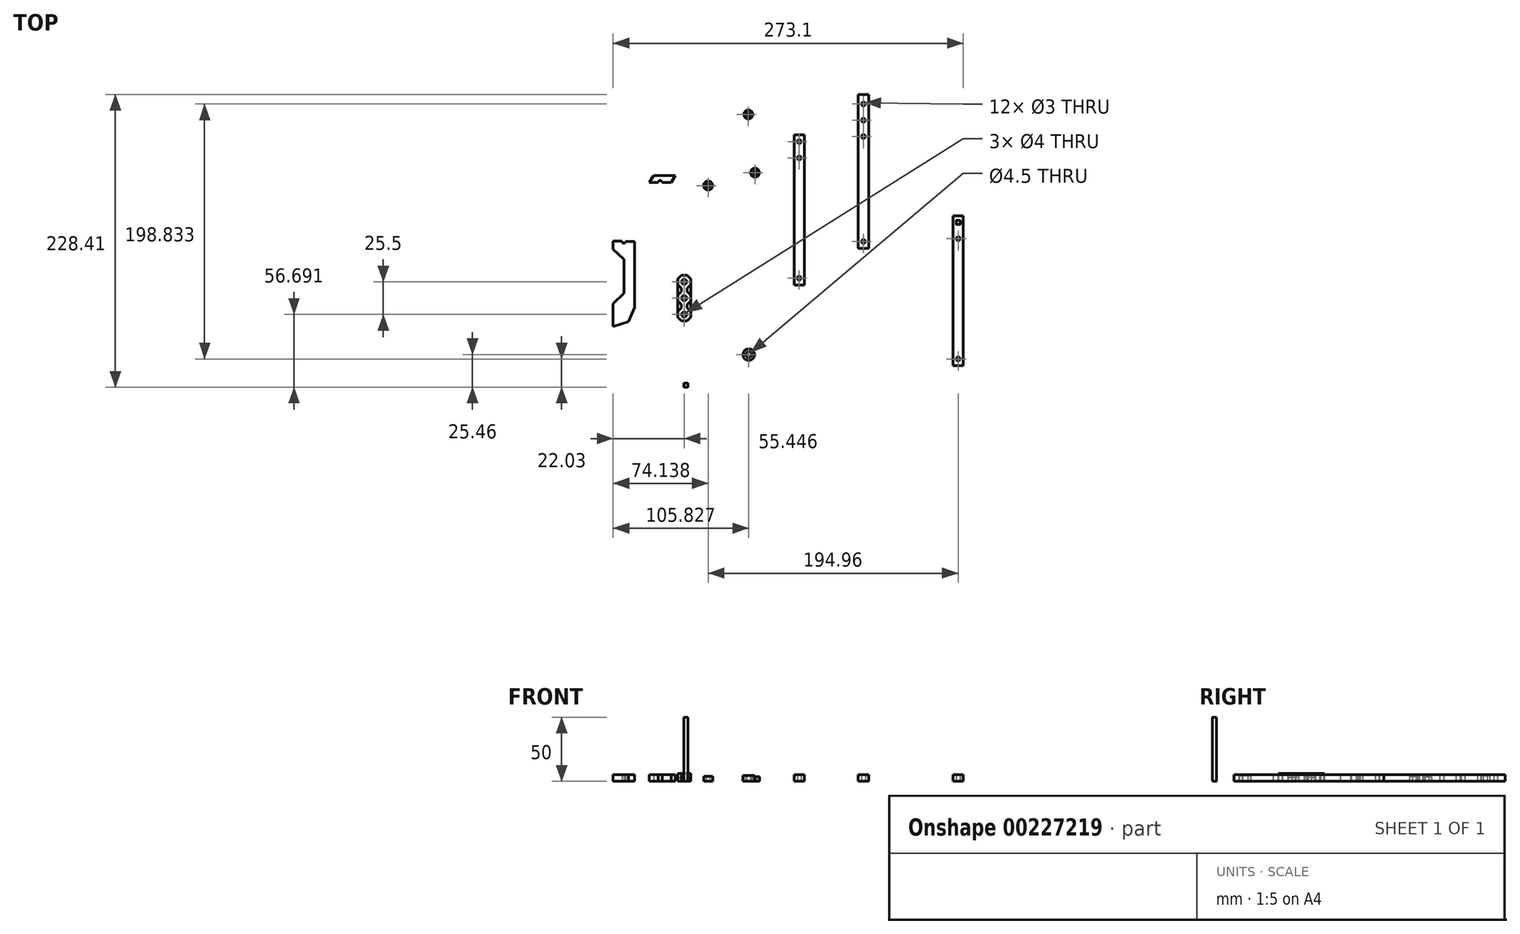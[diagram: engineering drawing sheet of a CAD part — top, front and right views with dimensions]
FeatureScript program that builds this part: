
annotation { "Feature Type Name" : "Feature", "Feature Type Description" : "" }
export const myFeature = defineFeature(function(context is Context, id is Id, definition is map)
    precondition{}
    {
        {
            var Q0;
            Q0=qCreatedBy(makeId("Top.planeOp"),FACE);
            var sketch = newSketch(context, id + "F0", { "sketchPlane" : qUnion([Q0])});
            skLineSegment(sketch, "E0", {"start": v(-67.95, 43.9) * mm, "end": v(-50.95, 43.9) * mm});
            skLineSegment(sketch, "E1", {"start": v(-67.95, 43.9) * mm, "end": v(-99.55, -7.1) * mm});
            skLineSegment(sketch, "E2", {"start": v(-50.95, 43.9) * mm, "end": v(-82.81, -7.53) * mm});
            skLineSegment(sketch, "E3", {"start": v(-99.55, -7.1) * mm, "end": v(-99.55, -13.4) * mm});
            skLineSegment(sketch, "E4", {"start": v(-82.81, -7.53) * mm, "end": v(-82.81, -59.03) * mm});
            skLineSegment(sketch, "E5", {"start": v(-82.81, -59.03) * mm, "end": v(-87.58, -70.04) * mm});
            skLineSegment(sketch, "E6", {"start": v(-87.58, -70.04) * mm, "end": v(-99.57, -73.9) * mm});
            skLineSegment(sketch, "E7", {"start": v(-99.57, -73.9) * mm, "end": v(-99.57, -55.9) * mm});
            skLineSegment(sketch, "E8", {"start": v(-99.55, -13.4) * mm, "end": v(-90.95, -13.4) * mm});
            skLineSegment(sketch, "E9", {"start": v(-90.95, -13.4) * mm, "end": v(-90.95, -55.9) * mm});
            skLineSegment(sketch, "E10", {"start": v(-90.95, -55.9) * mm, "end": v(-99.57, -55.9) * mm});
            skLineSegment(sketch, "E11", {"start": v(-99.55, -13.4) * mm, "end": v(-90.95, -21.4) * mm});
            skLineSegment(sketch, "E12", {"start": v(-99.57, -55.9) * mm, "end": v(-90.95, -47.88) * mm});
            skLineSegment(sketch, "E13", {"start": v(-99.55, -7.1) * mm, "end": v(-82.81, -7.53) * mm});
            skCircle(sketch, "E14", {"center": v(-91.18, -7.32) * mm, "radius": 1.5 * mm});
            skLineSegment(sketch, "E15", {"start": v(-71.24, 38.6) * mm, "end": v(-54.24, 38.6) * mm});
            skCircle(sketch, "E16", {"center": v(-62.74, 38.6) * mm, "radius": 1.5 * mm});
            skLineSegment(sketch, "E17", {"start": v(45.58, 70.38) * mm, "end": v(45.58, -36.08) * mm});
            skCircle(sketch, "E18", {"center": v(45.58, 70.38) * mm, "radius": 1.5 * mm});
            skCircle(sketch, "E19", {"center": v(45.58, -36.08) * mm, "radius": 1.5 * mm});
            skLineSegment(sketch, "E20.bottom", {"start": v(49.58, 75.65) * mm, "end": v(41.58, 75.65) * mm});
            skLineSegment(sketch, "E20.top", {"start": v(49.58, -41.35) * mm, "end": v(41.58, -41.35) * mm});
            skLineSegment(sketch, "E20.left", {"start": v(49.58, 75.65) * mm, "end": v(49.58, -41.35) * mm});
            skLineSegment(sketch, "E20.right", {"start": v(41.58, 75.65) * mm, "end": v(41.58, -41.35) * mm});
            skPoint(sketch, "E20.middle", {"position": v(45.58, 17.15) * mm});
            skLineSegment(sketch, "E21", {"start": v(95.66, 87.02) * mm, "end": v(95.66, -7.48) * mm});
            skCircle(sketch, "E22", {"center": v(95.66, 87.02) * mm, "radius": 1.5 * mm});
            skCircle(sketch, "E23", {"center": v(95.66, -7.48) * mm, "radius": 1.5 * mm});
            skLineSegment(sketch, "E24.bottom", {"start": v(99.66, 92.27) * mm, "end": v(91.66, 92.27) * mm});
            skLineSegment(sketch, "E24.top", {"start": v(99.66, -12.73) * mm, "end": v(91.66, -12.73) * mm});
            skLineSegment(sketch, "E24.left", {"start": v(99.66, 92.27) * mm, "end": v(99.66, -12.73) * mm});
            skLineSegment(sketch, "E24.right", {"start": v(91.66, 92.27) * mm, "end": v(91.66, -12.73) * mm});
            skPoint(sketch, "E24.middle", {"position": v(95.66, 39.77) * mm});
            skCircle(sketch, "E25", {"center": v(-42.75, -119.57) * mm, "radius": 1.5 * mm});
            skCircle(sketch, "E26", {"center": v(5.9, 91.64) * mm, "radius": 1.5 * mm});
            skCircle(sketch, "E27", {"center": v(5.9, 91.64) * mm, "radius": 3.5 * mm});
            skCircle(sketch, "E28", {"center": v(29.29, -65.49) * mm, "radius": 3.14 * mm});
            skLineSegment(sketch, "E29", {"start": v(169.53, -99.11) * mm, "end": v(169.53, 7.39) * mm});
            skLineSegment(sketch, "E30.bottom", {"start": v(173.53, 12.64) * mm, "end": v(165.53, 12.64) * mm});
            skLineSegment(sketch, "E30.top", {"start": v(173.53, -104.36) * mm, "end": v(165.53, -104.36) * mm});
            skLineSegment(sketch, "E30.left", {"start": v(173.53, 12.64) * mm, "end": v(173.53, -104.36) * mm});
            skLineSegment(sketch, "E30.right", {"start": v(165.53, 12.64) * mm, "end": v(165.53, -104.36) * mm});
            skPoint(sketch, "E30.middle", {"position": v(169.53, -45.86) * mm});
            skLineSegment(sketch, "E31.bottom", {"start": v(171.13, 8.99) * mm, "end": v(167.93, 8.99) * mm});
            skLineSegment(sketch, "E31.top", {"start": v(171.13, 5.79) * mm, "end": v(167.93, 5.79) * mm});
            skLineSegment(sketch, "E31.left", {"start": v(171.13, 8.99) * mm, "end": v(171.13, 5.79) * mm});
            skLineSegment(sketch, "E31.right", {"start": v(167.93, 8.99) * mm, "end": v(167.93, 5.79) * mm});
            skPoint(sketch, "E31.middle", {"position": v(169.53, 7.39) * mm});
            skCircle(sketch, "E32", {"center": v(169.53, -99.11) * mm, "radius": 1.5 * mm});
            skLineSegment(sketch, "E33.bottom", {"start": v(-41.18, -121.14) * mm, "end": v(-44.33, -121.14) * mm});
            skLineSegment(sketch, "E33.top", {"start": v(-41.18, -118) * mm, "end": v(-44.33, -118) * mm});
            skLineSegment(sketch, "E33.left", {"start": v(-41.18, -121.14) * mm, "end": v(-41.18, -118) * mm});
            skLineSegment(sketch, "E33.right", {"start": v(-44.33, -121.14) * mm, "end": v(-44.33, -118) * mm});
            skCircle(sketch, "E34", {"center": v(169.53, 7.39) * mm, "radius": 2.1 * mm});
            skLineSegment(sketch, "E35.bottom", {"start": v(165.53, 12.64) * mm, "end": v(173.53, 12.64) * mm});
            skLineSegment(sketch, "E35.top", {"start": v(165.53, 27.64) * mm, "end": v(173.53, 27.64) * mm});
            skLineSegment(sketch, "E35.left", {"start": v(165.53, 12.64) * mm, "end": v(165.53, 27.64) * mm});
            skLineSegment(sketch, "E35.right", {"start": v(173.53, 12.64) * mm, "end": v(173.53, 27.64) * mm});
            skCircle(sketch, "E36", {"center": v(169.53, 20.09) * mm, "radius": 1.5 * mm});
            skPoint(sketch, "E36.centerSnap0", {"position": v(169.53, 12.64) * mm});
            skCircle(sketch, "E37", {"center": v(169.53, -5.31) * mm, "radius": 1.5 * mm});
            skLineSegment(sketch, "E38.bottom", {"start": v(41.58, 75.65) * mm, "end": v(49.58, 75.65) * mm});
            skLineSegment(sketch, "E38.top", {"start": v(41.58, 90.65) * mm, "end": v(49.58, 90.65) * mm});
            skLineSegment(sketch, "E38.left", {"start": v(41.58, 75.65) * mm, "end": v(41.58, 90.65) * mm});
            skLineSegment(sketch, "E38.right", {"start": v(49.58, 75.65) * mm, "end": v(49.58, 90.65) * mm});
            skCircle(sketch, "E39", {"center": v(45.58, 83.08) * mm, "radius": 1.5 * mm});
            skPoint(sketch, "E39.centerSnap0", {"position": v(45.58, 75.65) * mm});
            skCircle(sketch, "E40", {"center": v(45.58, 57.68) * mm, "radius": 1.5 * mm});
            skLineSegment(sketch, "E41", {"start": v(91.66, 92.27) * mm, "end": v(91.66, 107.27) * mm});
            skLineSegment(sketch, "E42", {"start": v(91.66, 107.27) * mm, "end": v(99.66, 107.27) * mm});
            skLineSegment(sketch, "E43", {"start": v(99.66, 107.27) * mm, "end": v(99.66, 92.27) * mm});
            skCircle(sketch, "E44", {"center": v(95.66, 99.72) * mm, "radius": 1.5 * mm});
            skCircle(sketch, "E45", {"center": v(95.66, 74.32) * mm, "radius": 1.5 * mm});
            skCircle(sketch, "E46", {"center": v(6.26, -95.68) * mm, "radius": 2.25 * mm});
            skCircle(sketch, "E47", {"center": v(6.26, -95.68) * mm, "radius": 4.5 * mm});
            skLineSegment(sketch, "E48", {"start": v(-91.18, -7.32) * mm, "end": v(-62.74, -7.32) * mm, "construction": true});
            skLineSegment(sketch, "E49", {"start": v(-62.74, -7.32) * mm, "end": v(-62.74, 38.6) * mm, "construction": true});
            skLineSegment(sketch, "E50", {"start": v(-91.18, -7.32) * mm, "end": v(-62.74, 38.6) * mm, "construction": true});
            skSolve(sketch);
        }
        {
            var Q0;
            Q0=makeQuery(id+"F0.imprint","IMPRINT",FACE,{"disambiguationData":[TD([[makeQuery(id+"F0.imprint","IMPRINT",EDGE,{"derivedFrom":sQuery(id+"F0.wireOp",EDGE,"E0")}),-1.0]])]});
            var Q1;
            {var subQ0=sQuery(id+"F0.wireOp",EDGE,"E8");Q1=makeQuery(id+"F0.imprint","IMPRINT",FACE,{"disambiguationData":[TD([[makeQuery(id+"F0.imprint","IMPRINT",EDGE,{"derivedFrom":subQ0}),-1.0]])]});}
            var Q2;
            {var subQ0=sQuery(id+"F0.wireOp",EDGE,"E10");Q2=makeQuery(id+"F0.imprint","IMPRINT",FACE,{"disambiguationData":[TD([[makeQuery(id+"F0.imprint","IMPRINT",EDGE,{"derivedFrom":subQ0}),-1.0]])]});}
            var Q3;
            {var subQ0=sQuery(id+"F0.wireOp",EDGE,"E13");var subQ3=sQuery(id+"F0.wireOp",EDGE,"E14");var subQ12=makeQuery(id+"F0.imprint","INTERSECT",VERTEX,{"disambiguationData":[OD(0.0)],"derivedFrom":[subQ0,subQ3]});Q3=makeQuery(id+"F0.imprint","IMPRINT",FACE,{"disambiguationData":[TD([[makeQuery(id+"F0.imprint","IMPRINT",EDGE,{"disambiguationData":[TD([[subQ12,1.0]])],"derivedFrom":subQ3}),-1.0]])]});}
            var Q4;
            {var subQ5=sQuery(id+"F0.wireOp",EDGE,"E3");Q4=makeQuery(id+"F0.imprint","IMPRINT",FACE,{"disambiguationData":[TD([[makeQuery(id+"F0.imprint","IMPRINT",EDGE,{"derivedFrom":subQ5}),1.0]])]});}
            var Q5;
            Q5=makeQuery(id+"F0.imprint","IMPRINT",FACE,{"disambiguationData":[TD([[makeQuery(id+"F0.imprint","IMPRINT",EDGE,{"derivedFrom":sQuery(id+"F0.wireOp",EDGE,"E18")}),-1.0]])]});
            var Q6;
            Q6=makeQuery(id+"F0.imprint","IMPRINT",FACE,{"disambiguationData":[TD([[makeQuery(id+"F0.imprint","IMPRINT",EDGE,{"derivedFrom":sQuery(id+"F0.wireOp",EDGE,"E22")}),-1.0]])]});
            var Q7;
            {var subQ0=sQuery(id+"F0.wireOp",EDGE,"E34");var subQ1=sQuery(id+"F0.wireOp",EDGE,"E31.bottom");var subQ2=makeQuery(id+"F0.imprint","INTERSECT",VERTEX,{"disambiguationData":[OD(0.0)],"derivedFrom":[subQ1,subQ0]});Q7=makeQuery(id+"F0.imprint","IMPRINT",FACE,{"disambiguationData":[TD([[makeQuery(id+"F0.imprint","IMPRINT",EDGE,{"disambiguationData":[TD([[subQ2,-1.0]])],"derivedFrom":subQ1}),-1.0]])]});}
            var Q8;
            {var subQ0=sQuery(id+"F0.wireOp",EDGE,"E34");var subQ1=sQuery(id+"F0.wireOp",EDGE,"E31.right");var subQ2=makeQuery(id+"F0.imprint","INTERSECT",VERTEX,{"disambiguationData":[OD(0.0)],"derivedFrom":[subQ1,subQ0]});Q8=makeQuery(id+"F0.imprint","IMPRINT",FACE,{"disambiguationData":[TD([[makeQuery(id+"F0.imprint","IMPRINT",EDGE,{"disambiguationData":[TD([[subQ2,-1.0]])],"derivedFrom":subQ1}),-1.0]])]});}
            var Q9;
            {var subQ0=sQuery(id+"F0.wireOp",EDGE,"E34");var subQ1=sQuery(id+"F0.wireOp",EDGE,"E31.left");var subQ2=makeQuery(id+"F0.imprint","INTERSECT",VERTEX,{"disambiguationData":[OD(0.0)],"derivedFrom":[subQ1,subQ0]});Q9=makeQuery(id+"F0.imprint","IMPRINT",FACE,{"disambiguationData":[TD([[makeQuery(id+"F0.imprint","IMPRINT",EDGE,{"disambiguationData":[TD([[subQ2,-1.0]])],"derivedFrom":subQ1}),1.0]])]});}
            var Q10;
            {var subQ0=sQuery(id+"F0.wireOp",EDGE,"E31.top");var subQ1=sQuery(id+"F0.wireOp",EDGE,"E29");var subQ2=makeQuery(id+"F0.imprint","INTERSECT",VERTEX,{"derivedFrom":[subQ1,subQ0]});Q10=makeQuery(id+"F0.imprint","IMPRINT",FACE,{"disambiguationData":[TD([[makeQuery(id+"F0.imprint","IMPRINT",EDGE,{"disambiguationData":[TD([[subQ2,1.0]])],"derivedFrom":subQ1}),-1.0]])]});}
            var Q11;
            {var subQ0=sQuery(id+"F0.wireOp",EDGE,"E31.top");var subQ1=sQuery(id+"F0.wireOp",EDGE,"E29");var subQ2=makeQuery(id+"F0.imprint","INTERSECT",VERTEX,{"derivedFrom":[subQ1,subQ0]});Q11=makeQuery(id+"F0.imprint","IMPRINT",FACE,{"disambiguationData":[TD([[makeQuery(id+"F0.imprint","IMPRINT",EDGE,{"disambiguationData":[TD([[subQ2,1.0]])],"derivedFrom":subQ1}),1.0]])]});}
            var Q12;
            Q12=makeQuery(id+"F0.imprint","IMPRINT",FACE,{"disambiguationData":[TD([[makeQuery(id+"F0.imprint","IMPRINT",EDGE,{"derivedFrom":sQuery(id+"F0.wireOp",EDGE,"E30.bottom")}),1.0]])]});
            var Q13;
            {var subQ0=sQuery(id+"F0.wireOp",EDGE,"E31.left");var subQ1=sQuery(id+"F0.wireOp",EDGE,"E31.bottom");var subQ2=makeQuery(id+"F0.imprint","INTERSECT",VERTEX,{"derivedFrom":[subQ1,subQ0]});Q13=makeQuery(id+"F0.imprint","IMPRINT",FACE,{"disambiguationData":[TD([[makeQuery(id+"F0.imprint","IMPRINT",EDGE,{"disambiguationData":[TD([[subQ2,-1.0]])],"derivedFrom":subQ1}),1.0]])]});}
            var Q14;
            {var subQ0=sQuery(id+"F0.wireOp",EDGE,"E31.right");var subQ1=sQuery(id+"F0.wireOp",EDGE,"E31.bottom");var subQ2=makeQuery(id+"F0.imprint","INTERSECT",VERTEX,{"derivedFrom":[subQ1,subQ0]});Q14=makeQuery(id+"F0.imprint","IMPRINT",FACE,{"disambiguationData":[TD([[makeQuery(id+"F0.imprint","IMPRINT",EDGE,{"disambiguationData":[TD([[subQ2,1.0]])],"derivedFrom":subQ1}),1.0]])]});}
            var Q15;
            {var subQ0=sQuery(id+"F0.wireOp",EDGE,"E31.right");var subQ1=sQuery(id+"F0.wireOp",EDGE,"E31.top");var subQ2=makeQuery(id+"F0.imprint","INTERSECT",VERTEX,{"derivedFrom":[subQ1,subQ0]});Q15=makeQuery(id+"F0.imprint","IMPRINT",FACE,{"disambiguationData":[TD([[makeQuery(id+"F0.imprint","IMPRINT",EDGE,{"disambiguationData":[TD([[subQ2,1.0]])],"derivedFrom":subQ1}),-1.0]])]});}
            var Q16;
            {var subQ0=sQuery(id+"F0.wireOp",EDGE,"E31.left");var subQ1=sQuery(id+"F0.wireOp",EDGE,"E31.top");var subQ2=makeQuery(id+"F0.imprint","INTERSECT",VERTEX,{"derivedFrom":[subQ1,subQ0]});Q16=makeQuery(id+"F0.imprint","IMPRINT",FACE,{"disambiguationData":[TD([[makeQuery(id+"F0.imprint","IMPRINT",EDGE,{"disambiguationData":[TD([[subQ2,-1.0]])],"derivedFrom":subQ1}),-1.0]])]});}
            var Q17;
            Q17=makeQuery(id+"F0.imprint","IMPRINT",FACE,{"disambiguationData":[TD([[makeQuery(id+"F0.imprint","IMPRINT",EDGE,{"derivedFrom":sQuery(id+"F0.wireOp",EDGE,"E35.bottom")}),1.0]])]});
            var Q18;
            Q18=makeQuery(id+"F0.imprint","IMPRINT",FACE,{"disambiguationData":[TD([[makeQuery(id+"F0.imprint","IMPRINT",EDGE,{"derivedFrom":sQuery(id+"F0.wireOp",EDGE,"E30.top")}),-1.0]])]});
            var Q19;
            Q19=makeQuery(id+"F0.imprint","IMPRINT",FACE,{"disambiguationData":[TD([[makeQuery(id+"F0.imprint","IMPRINT",EDGE,{"derivedFrom":sQuery(id+"F0.wireOp",EDGE,"E38.bottom")}),1.0]])]});
            var Q20;
            Q20=makeQuery(id+"F0.imprint","IMPRINT",FACE,{"disambiguationData":[TD([[makeQuery(id+"F0.imprint","IMPRINT",EDGE,{"derivedFrom":sQuery(id+"F0.wireOp",EDGE,"E24.bottom")}),-1.0]])]});
            extrude(context, id + "F1", {"entities" : qUnion([Q0, Q1, Q2, Q3, Q4, Q5, Q6, Q7, Q8, Q9, Q10, Q11, Q12, Q13, Q14, Q15, Q16, Q17, Q18, Q19, Q20]), "depth" : 5.08 * mm});
        }
        {
            var Q0;
            Q0=makeQuery(id+"F0.imprint","IMPRINT",FACE,{"disambiguationData":[TD([[makeQuery(id+"F0.imprint","IMPRINT",EDGE,{"derivedFrom":sQuery(id+"F0.wireOp",EDGE,"E25")}),1.0]])]});
            var Q1;
            Q1=makeQuery(id+"F0.imprint","IMPRINT",FACE,{"disambiguationData":[TD([[makeQuery(id+"F0.imprint","IMPRINT",EDGE,{"derivedFrom":sQuery(id+"F0.wireOp",EDGE,"E25")}),-1.0]])]});
            extrude(context, id + "F2", {"entities" : qUnion([Q0, Q1]), "depth" : 50 * mm});
        }
        {
            var Q0;
            Q0=makeQuery(id+"F0.imprint","IMPRINT",FACE,{"disambiguationData":[TD([[makeQuery(id+"F0.imprint","IMPRINT",EDGE,{"derivedFrom":sQuery(id+"F0.wireOp",EDGE,"E26")}),-1.0]])]});
            var Q1;
            Q1 = qSketchRegion(id + "F5", true);
            var Q2;
            Q2=makeQuery(id+"F0.imprint","IMPRINT",FACE,{"disambiguationData":[TD([[makeQuery(id+"F0.imprint","IMPRINT",EDGE,{"derivedFrom":sQuery(id+"F0.wireOp",EDGE,"E46")}),-1.0]])]});
            extrude(context, id + "F3", {"entities" : qUnion([Q0, Q1, Q2]), "depth" : 4.45 * mm});
        }
        {
            var Q0;
            Q0=makeQuery(id+"F2.opExtrude","SWEPT_EDGE",EDGE,{"disambiguationData":[OSD([sQuery(id+"F0.wireOp",EDGE,"E33.bottom"),sQuery(id+"F0.wireOp",EDGE,"E33.left")])]});
            var Q1;
            Q1=makeQuery(id+"F2.opExtrude","SWEPT_EDGE",EDGE,{"disambiguationData":[OSD([sQuery(id+"F0.wireOp",EDGE,"E33.top"),sQuery(id+"F0.wireOp",EDGE,"E33.right")])]});
            var Q2;
            Q2=makeQuery(id+"F2.opExtrude","SWEPT_EDGE",EDGE,{"disambiguationData":[OSD([sQuery(id+"F0.wireOp",EDGE,"E33.bottom"),sQuery(id+"F0.wireOp",EDGE,"E33.right")])]});
            var Q3;
            Q3=makeQuery(id+"F2.opExtrude","SWEPT_EDGE",EDGE,{"disambiguationData":[OSD([sQuery(id+"F0.wireOp",EDGE,"E33.top"),sQuery(id+"F0.wireOp",EDGE,"E33.left")])]});
            fillet(context, id + "F4", {"entities" : qUnion([Q0, Q1, Q2, Q3]), "radius" : 0.25 * mm, "tangentPropagation" : true, "allowEdgeOverflow" : false});
        }
        {
            var Q0;
            Q0=qCreatedBy(makeId("Top.planeOp"),FACE);
            var sketch = newSketch(context, id + "F5", { "sketchPlane" : qUnion([Q0])});
            skCircle(sketch, "E51", {"center": v(-25.43, 36.16) * mm, "radius": 3.5 * mm});
            skCircle(sketch, "E52", {"center": v(-25.43, 36.16) * mm, "radius": 1.5 * mm});
            skCircle(sketch, "E53", {"center": v(11.1, 46.21) * mm, "radius": 3.5 * mm});
            skCircle(sketch, "E54", {"center": v(11.1, 46.21) * mm, "radius": 1.5 * mm});
            skSolve(sketch);
        }
        {
            var Q0;
            Q0=makeQuery(id+"F5.imprint","IMPRINT",FACE,{"disambiguationData":[TD([[makeQuery(id+"F5.imprint","IMPRINT",EDGE,{"derivedFrom":sQuery(id+"F5.wireOp",EDGE,"E51")}),1.0]])]});
            extrude(context, id + "F6", {"entities" : qUnion([Q0]), "depth" : 3.81 * mm});
        }
        {
            var Q0;
            Q0=qCreatedBy(makeId("Top.planeOp"),FACE);
            var sketch = newSketch(context, id + "F7", { "sketchPlane" : qUnion([Q0])});
            skCircle(sketch, "E55", {"center": v(-44.12, -38.95) * mm, "radius": 2 * mm});
            skCircle(sketch, "E56", {"center": v(-44.12, -51.7) * mm, "radius": 2 * mm});
            skCircle(sketch, "E57", {"center": v(-44.12, -64.45) * mm, "radius": 2 * mm});
            skLineSegment(sketch, "E58", {"start": v(-44.12, -51.7) * mm, "end": v(-44.12, -38.95) * mm});
            skLineSegment(sketch, "E59", {"start": v(-44.12, -51.7) * mm, "end": v(-44.12, -64.45) * mm});
            skLineSegment(sketch, "E60", {"start": v(-46.37, -33.85) * mm, "end": v(-41.87, -33.85) * mm});
            skLineSegment(sketch, "E61", {"start": v(-49.22, -41.2) * mm, "end": v(-49.22, -36.7) * mm});
            skLineSegment(sketch, "E62.MirrorCS", {"start": v(-39.02, -41.2) * mm, "end": v(-39.02, -36.7) * mm});
            skLineSegment(sketch, "E63", {"start": v(-49.22, -36.7) * mm, "end": v(-46.37, -33.85) * mm});
            skLineSegment(sketch, "E64", {"start": v(-41.87, -33.85) * mm, "end": v(-39.02, -36.7) * mm});
            skLineSegment(sketch, "E65", {"start": v(-44.12, -38.95) * mm, "end": v(-39.02, -38.95) * mm});
            skPoint(sketch, "E65.endSnap0", {"position": v(-39.02, -38.94) * mm});
            skLineSegment(sketch, "E66.MirrorCS", {"start": v(-46.37, -44.05) * mm, "end": v(-41.87, -44.05) * mm});
            skLineSegment(sketch, "E67", {"start": v(-49.22, -41.2) * mm, "end": v(-46.37, -44.05) * mm});
            skLineSegment(sketch, "E68", {"start": v(-41.87, -44.05) * mm, "end": v(-39.02, -41.2) * mm});
            skPoint(sketch, "E69.endSnap0", {"position": v(-44.12, -45.32) * mm});
            skLineSegment(sketch, "E70.MirrorCS", {"start": v(-46.37, -46.6) * mm, "end": v(-41.87, -46.6) * mm});
            skLineSegment(sketch, "E71.MirrorCS", {"start": v(-41.87, -46.6) * mm, "end": v(-39.02, -49.46) * mm});
            skLineSegment(sketch, "E72.MirrorCS", {"start": v(-49.22, -49.46) * mm, "end": v(-46.37, -46.6) * mm});
            skLineSegment(sketch, "E73.MirrorCS", {"start": v(-49.22, -49.46) * mm, "end": v(-49.22, -53.96) * mm});
            skLineSegment(sketch, "E74.MirrorCS", {"start": v(-49.22, -53.96) * mm, "end": v(-46.37, -56.8) * mm});
            skLineSegment(sketch, "E75.MirrorCS", {"start": v(-46.37, -56.8) * mm, "end": v(-41.87, -56.8) * mm});
            skLineSegment(sketch, "E76.MirrorCS", {"start": v(-41.87, -56.8) * mm, "end": v(-39.02, -53.96) * mm});
            skLineSegment(sketch, "E77.MirrorCS", {"start": v(-39.02, -49.46) * mm, "end": v(-39.02, -53.96) * mm});
            skLineSegment(sketch, "E78.MirrorCS", {"start": v(-46.37, -59.35) * mm, "end": v(-41.87, -59.35) * mm});
            skLineSegment(sketch, "E79.MirrorCS", {"start": v(-41.87, -59.35) * mm, "end": v(-39.02, -62.2) * mm});
            skLineSegment(sketch, "E80.MirrorCS", {"start": v(-39.02, -66.7) * mm, "end": v(-39.02, -62.2) * mm});
            skLineSegment(sketch, "E81.MirrorCS", {"start": v(-41.87, -69.55) * mm, "end": v(-39.02, -66.7) * mm});
            skLineSegment(sketch, "E82.MirrorCS", {"start": v(-49.22, -62.2) * mm, "end": v(-46.37, -59.35) * mm});
            skLineSegment(sketch, "E83.MirrorCS", {"start": v(-49.22, -66.7) * mm, "end": v(-49.22, -62.2) * mm});
            skLineSegment(sketch, "E84.MirrorCS", {"start": v(-49.22, -66.7) * mm, "end": v(-46.37, -69.55) * mm});
            skLineSegment(sketch, "E85.MirrorCS", {"start": v(-46.37, -69.55) * mm, "end": v(-41.87, -69.55) * mm});
            skLineSegment(sketch, "E86", {"start": v(-46.37, -46.6) * mm, "end": v(-46.37, -44.05) * mm});
            skLineSegment(sketch, "E87", {"start": v(-41.87, -44.05) * mm, "end": v(-41.87, -46.6) * mm});
            skLineSegment(sketch, "E88", {"start": v(-46.37, -56.8) * mm, "end": v(-46.37, -59.35) * mm});
            skLineSegment(sketch, "E89", {"start": v(-41.87, -56.8) * mm, "end": v(-41.87, -59.35) * mm});
            skLineSegment(sketch, "E90", {"start": v(-49.22, -49.46) * mm, "end": v(-49.22, -41.2) * mm});
            skLineSegment(sketch, "E91", {"start": v(-39.02, -41.2) * mm, "end": v(-39.02, -49.46) * mm});
            skLineSegment(sketch, "E92", {"start": v(-39.02, -53.96) * mm, "end": v(-39.02, -62.2) * mm});
            skLineSegment(sketch, "E93", {"start": v(-49.22, -53.96) * mm, "end": v(-49.22, -62.2) * mm});
            skSolve(sketch);
        }
        {
            var Q0;
            Q0=makeQuery(id+"F7.imprint","IMPRINT",FACE,{"disambiguationData":[TD([[makeQuery(id+"F7.imprint","IMPRINT",EDGE,{"derivedFrom":sQuery(id+"F7.wireOp",EDGE,"E68")}),-1.0]])]});
            var Q1;
            Q1=makeQuery(id+"F7.imprint","IMPRINT",FACE,{"disambiguationData":[TD([[makeQuery(id+"F7.imprint","IMPRINT",EDGE,{"derivedFrom":sQuery(id+"F7.wireOp",EDGE,"E67")}),-1.0]])]});
            var Q2;
            Q2=makeQuery(id+"F7.imprint","IMPRINT",FACE,{"disambiguationData":[TD([[makeQuery(id+"F7.imprint","IMPRINT",EDGE,{"derivedFrom":sQuery(id+"F7.wireOp",EDGE,"E74.MirrorCS")}),-1.0]])]});
            var Q3;
            Q3=makeQuery(id+"F7.imprint","IMPRINT",FACE,{"disambiguationData":[TD([[makeQuery(id+"F7.imprint","IMPRINT",EDGE,{"derivedFrom":sQuery(id+"F7.wireOp",EDGE,"E76.MirrorCS")}),-1.0]])]});
            extrude(context, id + "F8", {"entities" : qUnion([Q0, Q1, Q2, Q3]), "depth" : 3.1 * mm});
        }
        {
            var Q0;
            Q0=makeQuery(id+"F7.imprint","IMPRINT",FACE,{"disambiguationData":[TD([[makeQuery(id+"F7.imprint","IMPRINT",EDGE,{"derivedFrom":sQuery(id+"F7.wireOp",EDGE,"E60")}),-1.0]])]});
            var Q1;
            {var subQ5=sQuery(id+"F7.wireOp",EDGE,"E68");Q1=makeQuery(id+"F7.imprint","IMPRINT",FACE,{"disambiguationData":[TD([[makeQuery(id+"F7.imprint","IMPRINT",EDGE,{"derivedFrom":subQ5}),1.0]])]});}
            var Q2;
            {var subQ0=sQuery(id+"F7.wireOp",EDGE,"E71.MirrorCS");Q2=makeQuery(id+"F7.imprint","IMPRINT",FACE,{"disambiguationData":[TD([[makeQuery(id+"F7.imprint","IMPRINT",EDGE,{"derivedFrom":subQ0}),-1.0]])]});}
            var Q3;
            {var subQ0=sQuery(id+"F7.wireOp",EDGE,"E72.MirrorCS");Q3=makeQuery(id+"F7.imprint","IMPRINT",FACE,{"disambiguationData":[TD([[makeQuery(id+"F7.imprint","IMPRINT",EDGE,{"derivedFrom":subQ0}),-1.0]])]});}
            var Q4;
            Q4=makeQuery(id+"F7.imprint","IMPRINT",FACE,{"disambiguationData":[TD([[makeQuery(id+"F7.imprint","IMPRINT",EDGE,{"derivedFrom":sQuery(id+"F7.wireOp",EDGE,"E57")}),-1.0]])]});
            var Q5;
            {var subQ5=sQuery(id+"F7.wireOp",EDGE,"E86");Q5=makeQuery(id+"F7.imprint","IMPRINT",FACE,{"disambiguationData":[TD([[makeQuery(id+"F7.imprint","IMPRINT",EDGE,{"derivedFrom":subQ5}),-1.0]])]});}
            var Q6;
            {var subQ5=sQuery(id+"F7.wireOp",EDGE,"E87");Q6=makeQuery(id+"F7.imprint","IMPRINT",FACE,{"disambiguationData":[TD([[makeQuery(id+"F7.imprint","IMPRINT",EDGE,{"derivedFrom":subQ5}),-1.0]])]});}
            var Q7;
            {var subQ5=sQuery(id+"F7.wireOp",EDGE,"E88");Q7=makeQuery(id+"F7.imprint","IMPRINT",FACE,{"disambiguationData":[TD([[makeQuery(id+"F7.imprint","IMPRINT",EDGE,{"derivedFrom":subQ5}),1.0]])]});}
            var Q8;
            {var subQ5=sQuery(id+"F7.wireOp",EDGE,"E89");Q8=makeQuery(id+"F7.imprint","IMPRINT",FACE,{"disambiguationData":[TD([[makeQuery(id+"F7.imprint","IMPRINT",EDGE,{"derivedFrom":subQ5}),-1.0]])]});}
            extrude(context, id + "F9", {"entities" : qUnion([Q0, Q1, Q2, Q3, Q4, Q5, Q6, Q7, Q8]), "depth" : 6.15 * mm});
        }
        {
            var Q0;
            Q0=makeQuery(id+"F5.imprint","IMPRINT",FACE,{"disambiguationData":[TD([[makeQuery(id+"F5.imprint","IMPRINT",EDGE,{"derivedFrom":sQuery(id+"F5.wireOp",EDGE,"E53")}),1.0]])]});
            extrude(context, id + "F10", {"entities" : qUnion([Q0]), "depth" : 3.76 * mm});
        }
    });
